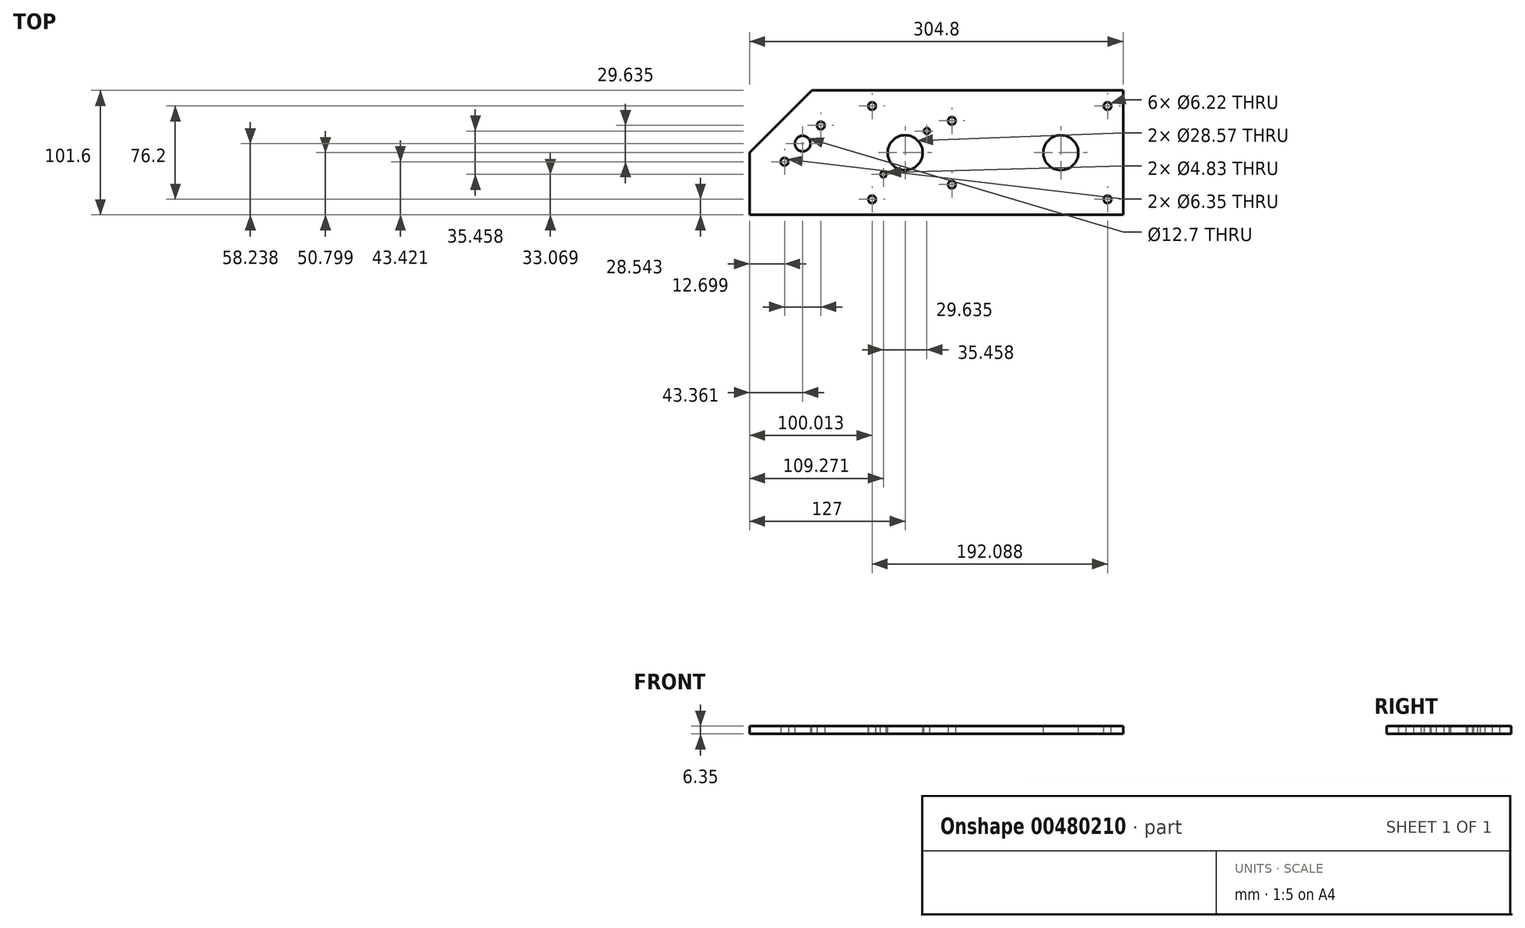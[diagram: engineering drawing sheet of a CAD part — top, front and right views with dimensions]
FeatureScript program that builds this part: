
annotation { "Feature Type Name" : "Feature", "Feature Type Description" : "" }
export const myFeature = defineFeature(function(context is Context, id is Id, definition is map)
    precondition{}
    {
        {
            var Q0;
            Q0=qCreatedBy(makeId("Top.planeOp"),FACE);
            var sketch = newSketch(context, id + "F0", { "sketchPlane" : qUnion([Q0])});
            skLineSegment(sketch, "E0.bottom", {"start": v(-72.69, 42.63) * mm, "end": v(232.11, 42.63) * mm});
            skLineSegment(sketch, "E0.top", {"start": v(-72.69, -58.97) * mm, "end": v(232.11, -58.97) * mm});
            skLineSegment(sketch, "E0.left", {"start": v(-72.69, 42.63) * mm, "end": v(-72.69, -58.97) * mm});
            skLineSegment(sketch, "E0.right", {"start": v(232.11, 42.63) * mm, "end": v(232.11, -58.97) * mm});
            skSolve(sketch);
        }
        {
            var Q0;
            Q0=makeQuery(id+"F0.imprint","IMPRINT",FACE,{"disambiguationData":[TD([[makeQuery(id+"F0.imprint","IMPRINT",EDGE,{"derivedFrom":sQuery(id+"F0.wireOp",EDGE,"E0.bottom")}),-1.0]])]});
            extrude(context, id + "F1", {"entities" : qUnion([Q0]), "depth" : 6.35 * mm});
        }
        {
            var Q0;
            Q0=makeQuery(id+"F1.opExtrude","CAP_FACE",FACE,{"disambiguationData":[OSD([sQuery(id+"F0.wireOp",EDGE,"E0.bottom"),sQuery(id+"F0.wireOp",EDGE,"E0.top"),sQuery(id+"F0.wireOp",EDGE,"E0.left"),sQuery(id+"F0.wireOp",EDGE,"E0.right")])],"isStart":false});
            var sketch = newSketch(context, id + "F2", { "sketchPlane" : qUnion([Q0])});
            skCircle(sketch, "E1", {"center": v(54.31, -8.17) * mm, "radius": 14.29 * mm});
            skSolve(sketch);
        }
        {
            var Q0;
            Q0=makeQuery(id+"F2.imprint","IMPRINT",FACE,{"disambiguationData":[TD([[makeQuery(id+"F2.imprint","IMPRINT",EDGE,{"derivedFrom":sQuery(id+"F2.wireOp",EDGE,"E1")}),1.0]])]});
            extrude(context, id + "F3", {"entities" : qUnion([Q0]), "operationType" : NewBodyOperationType.REMOVE, "oppositeDirection" : true, "depth" : 6.35 * mm});
        }
        {
            var Q0;
            Q0=makeQuery(id+"F1.opExtrude","CAP_FACE",FACE,{"disambiguationData":[OSD([sQuery(id+"F0.wireOp",EDGE,"E0.bottom"),sQuery(id+"F0.wireOp",EDGE,"E0.top"),sQuery(id+"F0.wireOp",EDGE,"E0.left"),sQuery(id+"F0.wireOp",EDGE,"E0.right")])],"isStart":false});
            var sketch = newSketch(context, id + "F4", { "sketchPlane" : qUnion([Q0])});
            skLineSegment(sketch, "E2.bottom", {"start": v(33.3, 14.05) * mm, "end": v(75.32, 14.05) * mm});
            skLineSegment(sketch, "E2.top", {"start": v(33.3, -30.4) * mm, "end": v(75.32, -30.4) * mm});
            skLineSegment(sketch, "E2.left", {"start": v(33.3, 14.05) * mm, "end": v(33.3, -30.4) * mm});
            skLineSegment(sketch, "E2.right", {"start": v(75.32, 14.05) * mm, "end": v(75.32, -30.4) * mm});
            skSolve(sketch);
        }
        {
            var Q0;
            Q0=makeQuery(id+"F4.imprint","IMPRINT",FACE,{"disambiguationData":[TD([[makeQuery(id+"F4.imprint","IMPRINT",EDGE,{"derivedFrom":sQuery(id+"F4.wireOp",EDGE,"E2.bottom")}),-1.0]])]});
            var sketch = newSketch(context, id + "F5", { "sketchPlane" : qUnion([Q0])});
            skCircle(sketch, "E3", {"center": v(36.58, -25.9) * mm, "radius": 2.41 * mm});
            skCircle(sketch, "E4", {"center": v(72.04, 9.56) * mm, "radius": 2.41 * mm});
            skSolve(sketch);
        }
        {
            var Q0;
            Q0=qSketchRegion(id+"F5",true);
            extrude(context, id + "F6", {"entities" : qUnion([Q0]), "operationType" : NewBodyOperationType.REMOVE, "oppositeDirection" : true, "depth" : 6.35 * mm});
        }
        {
            var Q0;
            Q0=makeQuery(id+"F0.imprint","IMPRINT",FACE,{"disambiguationData":[TD([[makeQuery(id+"F0.imprint","IMPRINT",EDGE,{"derivedFrom":sQuery(id+"F0.wireOp",EDGE,"E0.bottom")}),-1.0]])]});
            var sketch = newSketch(context, id + "F7", { "sketchPlane" : qUnion([Q0])});
            skCircle(sketch, "E5", {"center": v(27.32, 29.93) * mm, "radius": 3.11 * mm});
            skSolve(sketch);
        }
        {
            var Q0;
            Q0=makeQuery(id+"F7.imprint","IMPRINT",FACE,{"disambiguationData":[TD([[makeQuery(id+"F7.imprint","IMPRINT",EDGE,{"derivedFrom":sQuery(id+"F7.wireOp",EDGE,"E5")}),1.0]])]});
            extrude(context, id + "F8", {"entities" : qUnion([Q0]), "operationType" : NewBodyOperationType.REMOVE, "depth" : 6.35 * mm});
        }
        {
            var Q0;
            Q0=makeQuery(id+"F4.imprint","IMPRINT",FACE,{"disambiguationData":[TD([[makeQuery(id+"F4.imprint","IMPRINT",EDGE,{"derivedFrom":sQuery(id+"F4.wireOp",EDGE,"E2.bottom")}),1.0]])]});
            var sketch = newSketch(context, id + "F9", { "sketchPlane" : qUnion([Q0])});
            skCircle(sketch, "E6", {"center": v(219.41, 29.93) * mm, "radius": 3.11 * mm});
            skSolve(sketch);
        }
        {
            var Q0;
            Q0=makeQuery(id+"F9.imprint","IMPRINT",FACE,{"disambiguationData":[TD([[makeQuery(id+"F9.imprint","IMPRINT",EDGE,{"derivedFrom":sQuery(id+"F9.wireOp",EDGE,"E6")}),1.0]])]});
            extrude(context, id + "F10", {"entities" : qUnion([Q0]), "operationType" : NewBodyOperationType.REMOVE, "oppositeDirection" : true, "depth" : 6.35 * mm});
        }
        {
            var Q0;
            Q0=makeQuery(id+"F1.opExtrude","CAP_FACE",FACE,{"disambiguationData":[OSD([sQuery(id+"F0.wireOp",EDGE,"E0.bottom"),sQuery(id+"F0.wireOp",EDGE,"E0.top"),sQuery(id+"F0.wireOp",EDGE,"E0.left"),sQuery(id+"F0.wireOp",EDGE,"E0.right")])],"isStart":false});
            var sketch = newSketch(context, id + "F11", { "sketchPlane" : qUnion([Q0])});
            skCircle(sketch, "E7", {"center": v(27.33, -46.27) * mm, "radius": 3.11 * mm});
            skSolve(sketch);
        }
        {
            var Q0;
            Q0=makeQuery(id+"F11.imprint","IMPRINT",FACE,{"disambiguationData":[TD([[makeQuery(id+"F11.imprint","IMPRINT",EDGE,{"derivedFrom":sQuery(id+"F11.wireOp",EDGE,"E7")}),1.0]])]});
            extrude(context, id + "F12", {"entities" : qUnion([Q0]), "operationType" : NewBodyOperationType.REMOVE, "oppositeDirection" : true, "depth" : 6.35 * mm});
        }
        {
            var Q0;
            Q0=makeQuery(id+"F1.opExtrude","CAP_FACE",FACE,{"disambiguationData":[OSD([sQuery(id+"F0.wireOp",EDGE,"E0.bottom"),sQuery(id+"F0.wireOp",EDGE,"E0.top"),sQuery(id+"F0.wireOp",EDGE,"E0.left"),sQuery(id+"F0.wireOp",EDGE,"E0.right")])],"isStart":false});
            var sketch = newSketch(context, id + "F13", { "sketchPlane" : qUnion([Q0])});
            skCircle(sketch, "E8", {"center": v(219.41, -46.27) * mm, "radius": 3.11 * mm});
            skSolve(sketch);
        }
        {
            var Q0;
            Q0=makeQuery(id+"F13.imprint","IMPRINT",FACE,{"disambiguationData":[TD([[makeQuery(id+"F13.imprint","IMPRINT",EDGE,{"derivedFrom":sQuery(id+"F13.wireOp",EDGE,"E8")}),1.0]])]});
            extrude(context, id + "F14", {"entities" : qUnion([Q0]), "operationType" : NewBodyOperationType.REMOVE, "oppositeDirection" : true, "depth" : 6.35 * mm});
        }
        {
            var Q0;
            Q0=makeQuery(id+"F4.imprint","IMPRINT",FACE,{"disambiguationData":[TD([[makeQuery(id+"F4.imprint","IMPRINT",EDGE,{"derivedFrom":sQuery(id+"F4.wireOp",EDGE,"E2.bottom")}),1.0]])]});
            var sketch = newSketch(context, id + "F15", { "sketchPlane" : qUnion([Q0])});
            skCircle(sketch, "E9", {"center": v(181.31, -8.17) * mm, "radius": 14.29 * mm});
            skSolve(sketch);
        }
        {
            var Q0;
            Q0=makeQuery(id+"F15.imprint","IMPRINT",FACE,{"disambiguationData":[TD([[makeQuery(id+"F15.imprint","IMPRINT",EDGE,{"derivedFrom":sQuery(id+"F15.wireOp",EDGE,"E9")}),1.0]])]});
            extrude(context, id + "F16", {"entities" : qUnion([Q0]), "operationType" : NewBodyOperationType.REMOVE, "oppositeDirection" : true, "depth" : 6.35 * mm});
        }
        {
            var Q0;
            Q0=qCreatedBy(makeId("Top.planeOp"),FACE);
            var sketch = newSketch(context, id + "F17", { "sketchPlane" : qUnion([Q0])});
            skCircle(sketch, "E10", {"center": v(92.41, 17.86) * mm, "radius": 3.11 * mm});
            skSolve(sketch);
        }
        {
            var Q0;
            Q0=qCreatedBy(makeId("Top.planeOp"),FACE);
            var sketch = newSketch(context, id + "F18", { "sketchPlane" : qUnion([Q0])});
            skCircle(sketch, "E11", {"center": v(92.41, -34.2) * mm, "radius": 3.11 * mm});
            skSolve(sketch);
        }
        {
            var Q0;
            Q0=makeQuery(id+"F17.imprint","IMPRINT",FACE,{"disambiguationData":[TD([[makeQuery(id+"F17.imprint","IMPRINT",EDGE,{"derivedFrom":sQuery(id+"F17.wireOp",EDGE,"E10")}),1.0]])]});
            extrude(context, id + "F19", {"entities" : qUnion([Q0]), "operationType" : NewBodyOperationType.REMOVE, "depth" : 6.35 * mm});
        }
        {
            var Q0;
            Q0=makeQuery(id+"F18.imprint","IMPRINT",FACE,{"disambiguationData":[TD([[makeQuery(id+"F18.imprint","IMPRINT",EDGE,{"derivedFrom":sQuery(id+"F18.wireOp",EDGE,"E11")}),1.0]])]});
            extrude(context, id + "F20", {"entities" : qUnion([Q0]), "operationType" : NewBodyOperationType.REMOVE, "depth" : 6.35 * mm});
        }
        {
            var Q0;
            Q0=makeQuery(id+"F1.opExtrude","SWEPT_EDGE",EDGE,{"disambiguationData":[OSD([sQuery(id+"F0.wireOp",EDGE,"E0.bottom"),sQuery(id+"F0.wireOp",EDGE,"E0.left")])]});
            chamfer(context, id + "F21", {"entities" : qUnion([Q0]), "width" : 50.8 * mm, "tangentPropagation" : true});
        }
        {
            var Q0;
            Q0=makeQuery(id+"F1.opExtrude","CAP_FACE",FACE,{"disambiguationData":[OSD([sQuery(id+"F0.wireOp",EDGE,"E0.bottom"),sQuery(id+"F0.wireOp",EDGE,"E0.top"),sQuery(id+"F0.wireOp",EDGE,"E0.left"),sQuery(id+"F0.wireOp",EDGE,"E0.right")])],"isStart":true});
            var sketch = newSketch(context, id + "F22", { "sketchPlane" : qUnion([Q0])});
            skLineSegment(sketch, "E12", {"start": v(-47.29, -17.23) * mm, "end": v(28.91, 58.97) * mm});
            skCircle(sketch, "E13", {"center": v(-29.33, 0.73) * mm, "radius": 6.35 * mm});
            skLineSegment(sketch, "E14", {"start": v(-29.33, 0.73) * mm, "end": v(-14.51, -14.09) * mm});
            skLineSegment(sketch, "E15", {"start": v(-29.33, 0.73) * mm, "end": v(-44.15, 15.55) * mm});
            skCircle(sketch, "E16", {"center": v(-44.15, 15.55) * mm, "radius": 3.18 * mm});
            skCircle(sketch, "E17", {"center": v(-14.51, -14.09) * mm, "radius": 3.17 * mm});
            skSolve(sketch);
        }
        {
            var Q0;
            Q0=makeQuery(id+"F22.imprint","IMPRINT",FACE,{"disambiguationData":[TD([[makeQuery(id+"F22.imprint","IMPRINT",EDGE,{"derivedFrom":sQuery(id+"F22.wireOp",EDGE,"E16")}),1.0]])]});
            var Q1;
            {var subQ0=sQuery(id+"F22.wireOp",EDGE,"E15");var subQ3=sQuery(id+"F22.wireOp",EDGE,"E13");var subQ5=makeQuery(id+"F22.imprint","INTERSECT",VERTEX,{"derivedFrom":[subQ3,subQ0]});Q1=makeQuery(id+"F22.imprint","IMPRINT",FACE,{"disambiguationData":[TD([[makeQuery(id+"F22.imprint","IMPRINT",EDGE,{"disambiguationData":[TD([[subQ5,1.0]])],"derivedFrom":subQ3}),1.0]])]});}
            var Q2;
            {var subQ0=sQuery(id+"F22.wireOp",EDGE,"E15");var subQ3=sQuery(id+"F22.wireOp",EDGE,"E13");var subQ5=makeQuery(id+"F22.imprint","INTERSECT",VERTEX,{"derivedFrom":[subQ3,subQ0]});Q2=makeQuery(id+"F22.imprint","IMPRINT",FACE,{"disambiguationData":[TD([[makeQuery(id+"F22.imprint","IMPRINT",EDGE,{"disambiguationData":[TD([[subQ5,-1.0]])],"derivedFrom":subQ3}),1.0]])]});}
            var Q3;
            {var subQ0=sQuery(id+"F22.wireOp",EDGE,"E14");var subQ3=sQuery(id+"F22.wireOp",EDGE,"E13");var subQ5=makeQuery(id+"F22.imprint","INTERSECT",VERTEX,{"derivedFrom":[subQ3,subQ0]});Q3=makeQuery(id+"F22.imprint","IMPRINT",FACE,{"disambiguationData":[TD([[makeQuery(id+"F22.imprint","IMPRINT",EDGE,{"disambiguationData":[TD([[subQ5,1.0]])],"derivedFrom":subQ3}),1.0]])]});}
            var Q4;
            {var subQ0=sQuery(id+"F22.wireOp",EDGE,"E14");var subQ3=sQuery(id+"F22.wireOp",EDGE,"E13");var subQ5=makeQuery(id+"F22.imprint","INTERSECT",VERTEX,{"derivedFrom":[subQ3,subQ0]});Q4=makeQuery(id+"F22.imprint","IMPRINT",FACE,{"disambiguationData":[TD([[makeQuery(id+"F22.imprint","IMPRINT",EDGE,{"disambiguationData":[TD([[subQ5,-1.0]])],"derivedFrom":subQ3}),1.0]])]});}
            var Q5;
            Q5=makeQuery(id+"F22.imprint","IMPRINT",FACE,{"disambiguationData":[TD([[makeQuery(id+"F22.imprint","IMPRINT",EDGE,{"derivedFrom":sQuery(id+"F22.wireOp",EDGE,"E17")}),1.0]])]});
            extrude(context, id + "F23", {"entities" : qUnion([Q0, Q1, Q2, Q3, Q4, Q5]), "operationType" : NewBodyOperationType.REMOVE, "oppositeDirection" : true, "depth" : 6.35 * mm, "offsetDistance" : 25.4 * mm});
        }
    });
